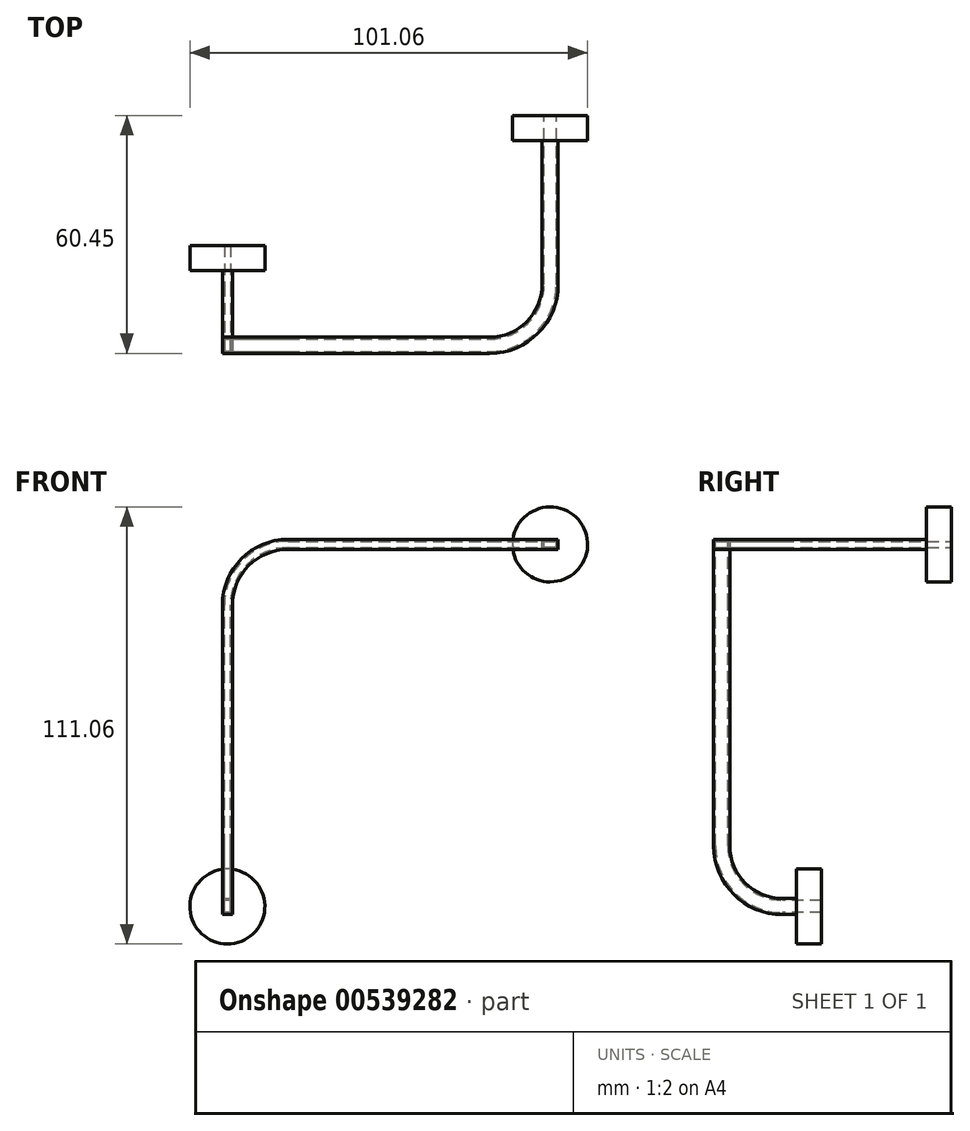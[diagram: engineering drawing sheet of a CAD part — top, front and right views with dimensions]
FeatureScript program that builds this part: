
annotation { "Feature Type Name" : "Feature", "Feature Type Description" : "" }
export const myFeature = defineFeature(function(context is Context, id is Id, definition is map)
    precondition{}
    {
        {
            var Q0;
            Q0=qCreatedBy(makeId("Top.planeOp"),FACE);
            var sketch = newSketch(context, id + "F0", { "sketchPlane" : qUnion([Q0])});
            skLineSegment(sketch, "E0", {"start": v(0, 0) * mm, "end": v(0, -10) * mm});
            skLineSegment(sketch, "E1", {"start": v(0, 0) * mm, "end": v(-25.4, 0) * mm});
            skLineSegment(sketch, "E2", {"start": v(-25.4, 0) * mm, "end": v(-25.4, -25.4) * mm});
            skLineSegment(sketch, "E3", {"start": v(-25.4, -25.4) * mm, "end": v(-15.4, -25.4) * mm});
            skArc(sketch, "E4", {"start": v(-15.4, -25.4) * mm, "mid": v(-4.51, -20.89) * mm, "end": v(0, -10) * mm});
            skLineSegment(sketch, "E5", {"start": v(-25.4, -25.4) * mm, "end": v(-56.6, -25.4) * mm});
            skLineSegment(sketch, "E6", {"start": v(0, 0) * mm, "end": v(0, 33) * mm});
            skSolve(sketch);
        }
        {
            var Q0;
            Q0=qCreatedBy(makeId("Front.planeOp"),FACE);
            cPlane(context, id + "F1", {"entities" : qUnion([Q0]), "cplaneType" : CPlaneType.OFFSET, "offset" : 25.4 * mm, "width" : 150 * mm, "height" : 150 * mm});
        }
        {
            var Q0;
            Q0=qCreatedBy(id+"F1.planeOp",FACE);
            var sketch = newSketch(context, id + "F2", { "sketchPlane" : qUnion([Q0])});
            skLineSegment(sketch, "E7", {"start": v(-56.6, 0) * mm, "end": v(-56.6, -25.4) * mm});
            skLineSegment(sketch, "E8", {"start": v(-56.6, -25.4) * mm, "end": v(-82, -25.4) * mm});
            skLineSegment(sketch, "E9", {"start": v(-56.6, 0) * mm, "end": v(-66.6, 0) * mm});
            skLineSegment(sketch, "E10", {"start": v(-82, -25.4) * mm, "end": v(-82, -15.4) * mm});
            skArc(sketch, "E11", {"start": v(-66.6, 0) * mm, "mid": v(-77.49, -4.51) * mm, "end": v(-82, -15.4) * mm});
            skLineSegment(sketch, "E12", {"start": v(-82, -25.4) * mm, "end": v(-82, -66.6) * mm});
            skSolve(sketch);
        }
        {
            var Q0;
            Q0=qCreatedBy(makeId("Right.planeOp"),FACE);
            cPlane(context, id + "F3", {"entities" : qUnion([Q0]), "cplaneType" : CPlaneType.OFFSET, "offset" : 82 * mm, "oppositeDirection" : true, "width" : 150 * mm, "height" : 150 * mm});
        }
        {
            var Q0;
            Q0=qCreatedBy(id+"F3.planeOp",FACE);
            var sketch = newSketch(context, id + "F4", { "sketchPlane" : qUnion([Q0])});
            skLineSegment(sketch, "E13", {"start": v(-25.4, -66.6) * mm, "end": v(0, -66.6) * mm});
            skLineSegment(sketch, "E14", {"start": v(0, -66.6) * mm, "end": v(0, -92) * mm});
            skLineSegment(sketch, "E15", {"start": v(-25.4, -66.6) * mm, "end": v(-25.4, -76.6) * mm});
            skLineSegment(sketch, "E16", {"start": v(0, -92) * mm, "end": v(-10, -92) * mm});
            skArc(sketch, "E17", {"start": v(-25.4, -76.6) * mm, "mid": v(-20.89, -87.49) * mm, "end": v(-10, -92) * mm});
            skSolve(sketch);
        }
        {
            var Q0;
            Q0=qCreatedBy(makeId("Front.planeOp"),FACE);
            cPlane(context, id + "F5", {"entities" : qUnion([Q0]), "cplaneType" : CPlaneType.OFFSET, "offset" : 33 * mm, "oppositeDirection" : true, "width" : 150 * mm, "height" : 150 * mm});
        }
        {
            var Q0;
            Q0=qCreatedBy(id+"F5.planeOp",FACE);
            var sketch = newSketch(context, id + "F6", { "sketchPlane" : qUnion([Q0])});
            skLineSegment(sketch, "E18.bottom", {"start": v(1.55, -0.77) * mm, "end": v(-1.55, -0.78) * mm});
            skLineSegment(sketch, "E18.top", {"start": v(1.55, 0.78) * mm, "end": v(-1.55, 0.78) * mm});
            skLineSegment(sketch, "E18.left", {"start": v(1.55, -0.77) * mm, "end": v(1.55, 0.78) * mm});
            skLineSegment(sketch, "E18.right", {"start": v(-1.55, -0.78) * mm, "end": v(-1.55, 0.78) * mm});
            skPoint(sketch, "E18.middle", {"position": v(0, 0) * mm});
            skLineSegment(sketch, "E19.bottom", {"start": v(2.05, -1.27) * mm, "end": v(-2.05, -1.27) * mm});
            skLineSegment(sketch, "E19.top", {"start": v(2.05, 1.27) * mm, "end": v(-2.05, 1.27) * mm});
            skLineSegment(sketch, "E19.left", {"start": v(2.05, -1.27) * mm, "end": v(2.05, 1.27) * mm});
            skLineSegment(sketch, "E19.right", {"start": v(-2.05, -1.27) * mm, "end": v(-2.05, 1.27) * mm});
            skCircle(sketch, "E20", {"center": v(0, 0) * mm, "radius": 9.53 * mm});
            skSolve(sketch);
        }
        {
            var Q0;
            Q0=qCreatedBy(makeId("Front.planeOp"),FACE);
            var sketch = newSketch(context, id + "F7", { "sketchPlane" : qUnion([Q0])});
            skLineSegment(sketch, "E21.bottom", {"start": v(-81.23, -93.55) * mm, "end": v(-82.78, -93.55) * mm});
            skLineSegment(sketch, "E21.top", {"start": v(-81.23, -90.45) * mm, "end": v(-82.78, -90.45) * mm});
            skLineSegment(sketch, "E21.left", {"start": v(-81.23, -93.55) * mm, "end": v(-81.23, -90.45) * mm});
            skLineSegment(sketch, "E21.right", {"start": v(-82.78, -93.55) * mm, "end": v(-82.78, -90.45) * mm});
            skPoint(sketch, "E21.middle", {"position": v(-82, -92) * mm});
            skLineSegment(sketch, "E22.bottom", {"start": v(-83.28, -94.05) * mm, "end": v(-80.73, -94.05) * mm});
            skLineSegment(sketch, "E22.top", {"start": v(-83.28, -89.95) * mm, "end": v(-80.73, -89.95) * mm});
            skLineSegment(sketch, "E22.left", {"start": v(-83.28, -94.05) * mm, "end": v(-83.28, -89.95) * mm});
            skLineSegment(sketch, "E22.right", {"start": v(-80.73, -94.05) * mm, "end": v(-80.73, -89.95) * mm});
            skCircle(sketch, "E23", {"center": v(-82, -92) * mm, "radius": 9.53 * mm});
            skSolve(sketch);
        }
        {
            var Q0;
            Q0=makeQuery(id+"F7.imprint","IMPRINT",FACE,{"disambiguationData":[TD([[makeQuery(id+"F7.imprint","IMPRINT",EDGE,{"derivedFrom":sQuery(id+"F7.wireOp",EDGE,"E21.bottom")}),1.0]])]});
            var Q1;
            Q1=sQuery(id+"F4.wireOp",EDGE,"E16");
            var Q2;
            Q2=sQuery(id+"F4.wireOp",EDGE,"E17");
            var Q3;
            Q3=sQuery(id+"F4.wireOp",EDGE,"E15");
            var Q4;
            Q4=sQuery(id+"F2.wireOp",EDGE,"E12");
            var Q5;
            Q5=sQuery(id+"F2.wireOp",EDGE,"E10");
            var Q6;
            Q6=sQuery(id+"F2.wireOp",EDGE,"E11");
            var Q7;
            Q7=sQuery(id+"F2.wireOp",EDGE,"E9");
            var Q8;
            Q8=sQuery(id+"F0.wireOp",EDGE,"E5");
            var Q9;
            Q9=sQuery(id+"F0.wireOp",EDGE,"E4");
            var Q10;
            Q10=sQuery(id+"F0.wireOp",EDGE,"E3");
            var Q11;
            Q11=sQuery(id+"F0.wireOp",EDGE,"E0");
            var Q12;
            Q12=sQuery(id+"F0.wireOp",EDGE,"E6");
            sweep(context, id + "F8", {"profiles" : qUnion([Q0]), "path" : qUnion([Q1, Q2, Q3, Q4, Q5, Q6, Q7, Q8, Q9, Q10, Q11, Q12])});
        }
        {
            var Q0;
            Q0=makeQuery(id+"F6.imprint","IMPRINT",FACE,{"disambiguationData":[TD([[makeQuery(id+"F6.imprint","IMPRINT",EDGE,{"derivedFrom":sQuery(id+"F6.wireOp",EDGE,"E19.bottom")}),1.0]])]});
            extrude(context, id + "F9", {"entities" : qUnion([Q0]), "operationType" : NewBodyOperationType.ADD, "depth" : 6.35 * mm, "offsetDistance" : 25 * mm});
        }
        {
            var Q0;
            Q0=makeQuery(id+"F7.imprint","IMPRINT",FACE,{"disambiguationData":[TD([[makeQuery(id+"F7.imprint","IMPRINT",EDGE,{"derivedFrom":sQuery(id+"F7.wireOp",EDGE,"E22.bottom")}),-1.0]])]});
            extrude(context, id + "F10", {"entities" : qUnion([Q0]), "operationType" : NewBodyOperationType.ADD, "depth" : 6.35 * mm, "offsetDistance" : 25 * mm});
        }
    });
